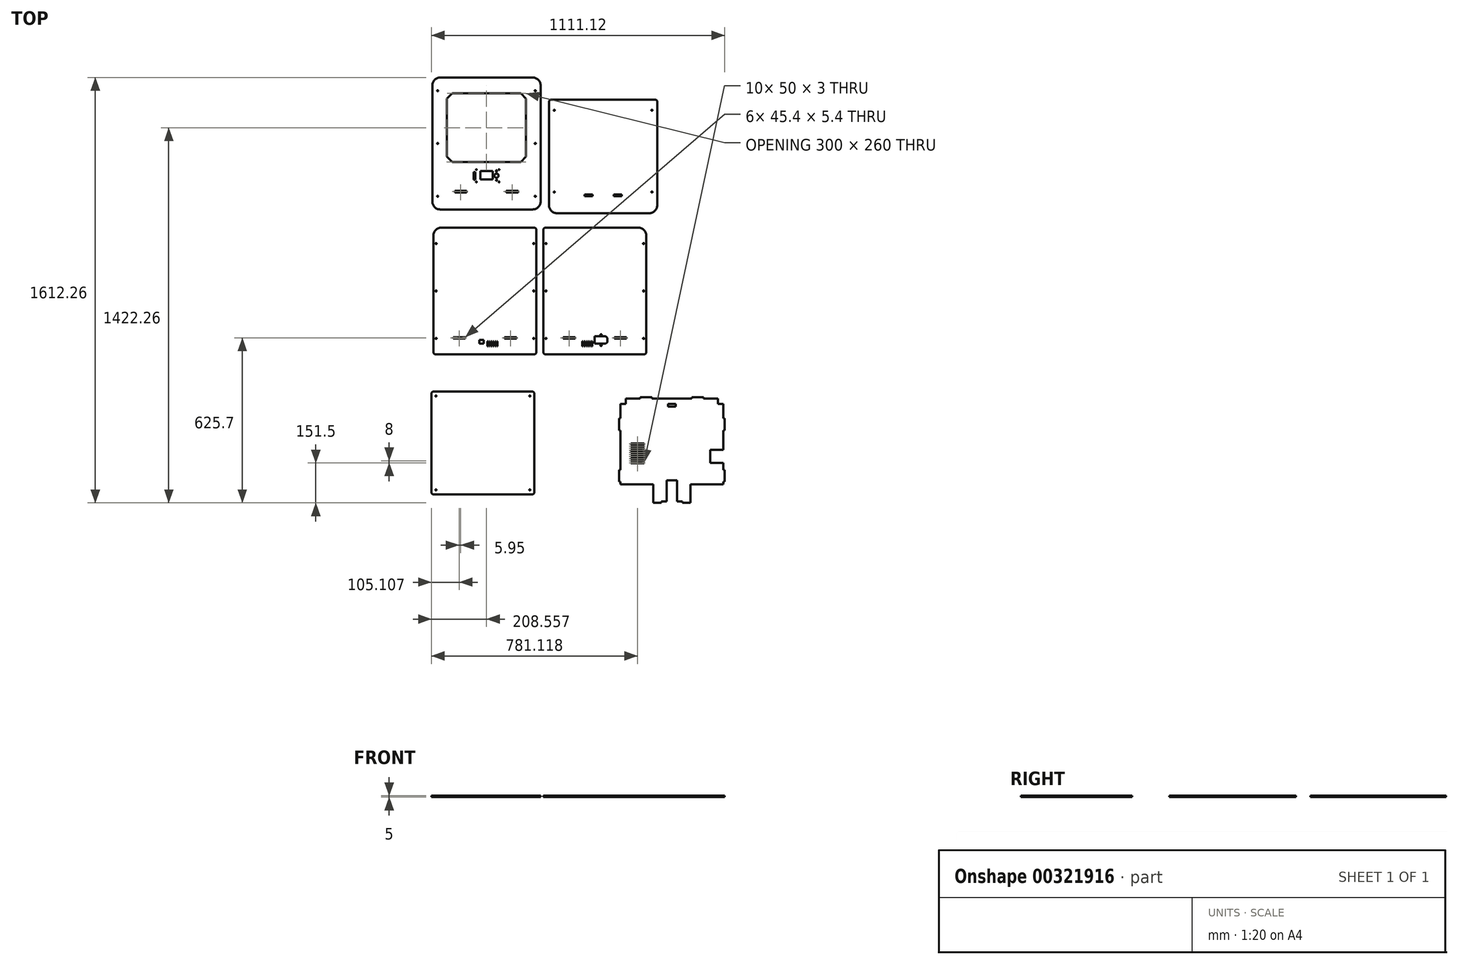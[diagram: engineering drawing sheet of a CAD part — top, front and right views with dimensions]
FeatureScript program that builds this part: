
annotation { "Feature Type Name" : "Feature", "Feature Type Description" : "" }
export const myFeature = defineFeature(function(context is Context, id is Id, definition is map)
    precondition{}
    {
        {
            var Q0;
            Q0=qCreatedBy(makeId("Top.planeOp"),FACE);
            var sketch = newSketch(context, id + "F0", { "sketchPlane" : qUnion([Q0])});
            skLineSegment(sketch, "E0.bottom", {"start": v(-407.26, 527.75) * mm, "end": v(2.74, 527.75) * mm});
            skLineSegment(sketch, "E0.top", {"start": v(-407.26, 27.75) * mm, "end": v(2.74, 27.75) * mm});
            skLineSegment(sketch, "E0.left", {"start": v(-407.26, 527.75) * mm, "end": v(-407.26, 27.75) * mm});
            skLineSegment(sketch, "E0.right", {"start": v(2.74, 527.75) * mm, "end": v(2.74, 27.75) * mm});
            skLineSegment(sketch, "E1.bottom", {"start": v(-352.26, 467.75) * mm, "end": v(-52.26, 467.75) * mm});
            skLineSegment(sketch, "E1.top", {"start": v(-352.26, 207.75) * mm, "end": v(-124.76, 207.75) * mm});
            skLineSegment(sketch, "E1.left", {"start": v(-352.26, 467.75) * mm, "end": v(-352.26, 207.75) * mm});
            skLineSegment(sketch, "E1.right", {"start": v(-52.26, 467.75) * mm, "end": v(-52.26, 207.75) * mm});
            skLineSegment(sketch, "E2", {"start": v(-124.76, 207.75) * mm, "end": v(-52.26, 207.75) * mm});
            skCircle(sketch, "E3", {"center": v(-387.26, 477.75) * mm, "radius": 2.1 * mm});
            skCircle(sketch, "E4", {"center": v(-17.26, 477.75) * mm, "radius": 2.1 * mm});
            skCircle(sketch, "E5", {"center": v(-387.26, 77.75) * mm, "radius": 2.1 * mm});
            skCircle(sketch, "E6", {"center": v(-17.26, 77.75) * mm, "radius": 2.1 * mm});
            skCircle(sketch, "E7", {"center": v(-387.26, 277.75) * mm, "radius": 2.1 * mm});
            skCircle(sketch, "E8", {"center": v(-17.26, 277.75) * mm, "radius": 2.1 * mm});
            skLineSegment(sketch, "E9.bottom", {"start": v(-322.46, 97.95) * mm, "end": v(-277.06, 97.95) * mm});
            skLineSegment(sketch, "E9.top", {"start": v(-322.46, 92.55) * mm, "end": v(-277.06, 92.55) * mm});
            skLineSegment(sketch, "E9.left", {"start": v(-322.46, 97.95) * mm, "end": v(-322.46, 92.55) * mm});
            skLineSegment(sketch, "E9.right", {"start": v(-277.06, 97.95) * mm, "end": v(-277.06, 92.55) * mm});
            skLineSegment(sketch, "E10.bottom", {"start": v(-127.46, 97.95) * mm, "end": v(-82.06, 97.95) * mm});
            skLineSegment(sketch, "E10.top", {"start": v(-127.46, 92.55) * mm, "end": v(-82.06, 92.55) * mm});
            skLineSegment(sketch, "E10.left", {"start": v(-127.46, 97.95) * mm, "end": v(-127.46, 92.55) * mm});
            skLineSegment(sketch, "E10.right", {"start": v(-82.06, 97.95) * mm, "end": v(-82.06, 92.55) * mm});
            skLineSegment(sketch, "E11.bottom", {"start": v(-225.86, 173.25) * mm, "end": v(-178.86, 173.25) * mm});
            skLineSegment(sketch, "E11.top", {"start": v(-225.86, 141.25) * mm, "end": v(-178.86, 141.25) * mm});
            skLineSegment(sketch, "E11.left", {"start": v(-225.86, 173.25) * mm, "end": v(-225.86, 141.25) * mm});
            skLineSegment(sketch, "E11.right", {"start": v(-178.86, 173.25) * mm, "end": v(-178.86, 141.25) * mm});
            skCircle(sketch, "E12", {"center": v(-164.36, 155.75) * mm, "radius": 8 * mm});
            skCircle(sketch, "E13", {"center": v(-164.36, 138.75) * mm, "radius": 2 * mm});
            skLineSegment(sketch, "E14.bottom", {"start": v(-250.86, 169.95) * mm, "end": v(-244.86, 169.95) * mm});
            skLineSegment(sketch, "E14.top", {"start": v(-250.86, 140.75) * mm, "end": v(-244.86, 140.75) * mm});
            skLineSegment(sketch, "E14.left", {"start": v(-250.86, 169.95) * mm, "end": v(-250.86, 140.75) * mm});
            skLineSegment(sketch, "E14.right", {"start": v(-244.86, 169.95) * mm, "end": v(-244.86, 140.75) * mm});
            skCircle(sketch, "E15", {"center": v(-164.36, 173.3) * mm, "radius": 0.6 * mm});
            skCircle(sketch, "E16", {"center": v(-167.36, 173.3) * mm, "radius": 0.6 * mm});
            skCircle(sketch, "E17", {"center": v(-164.36, 170.3) * mm, "radius": 0.6 * mm});
            skCircle(sketch, "E18", {"center": v(-161.36, 173.3) * mm, "radius": 0.6 * mm});
            skCircle(sketch, "E19", {"center": v(-164.36, 176.3) * mm, "radius": 0.6 * mm});
            skCircle(sketch, "E20", {"center": v(-154.56, 178.75) * mm, "radius": 1.6 * mm});
            skCircle(sketch, "E21", {"center": v(-154.56, 131.95) * mm, "radius": 1.6 * mm});
            skCircle(sketch, "E22", {"center": v(-240.56, 131.95) * mm, "radius": 1.6 * mm});
            skCircle(sketch, "E23", {"center": v(-240.56, 178.75) * mm, "radius": 1.6 * mm});
            skSolve(sketch);
        }
        {
            var Q0;
            Q0 = qSketchRegion(id + "F0", true);
            extrude(context, id + "F1", {"entities" : qUnion([Q0]), "offsetDistance" : 25 * mm, "depth" : 5 * mm});
        }
        {
            var Q0;
            Q0=makeQuery(id+"F1.opExtrude","SWEPT_EDGE",EDGE,{"disambiguationData":[OSD([sQuery(id+"F0.wireOp",EDGE,"E0.top"),sQuery(id+"F0.wireOp",EDGE,"E0.left")])]});
            var Q1;
            Q1=makeQuery(id+"F1.opExtrude","SWEPT_EDGE",EDGE,{"disambiguationData":[OSD([sQuery(id+"F0.wireOp",EDGE,"E0.top"),sQuery(id+"F0.wireOp",EDGE,"E0.right")])]});
            var Q2;
            Q2=makeQuery(id+"F1.opExtrude","SWEPT_EDGE",EDGE,{"disambiguationData":[OSD([sQuery(id+"F0.wireOp",EDGE,"E0.bottom"),sQuery(id+"F0.wireOp",EDGE,"E0.left")])]});
            var Q3;
            Q3=makeQuery(id+"F1.opExtrude","SWEPT_EDGE",EDGE,{"disambiguationData":[OSD([sQuery(id+"F0.wireOp",EDGE,"E0.bottom"),sQuery(id+"F0.wireOp",EDGE,"E0.right")])]});
            fillet(context, id + "F2", {"entities" : qUnion([Q0, Q1, Q2, Q3]), "radius" : 30 * mm, "tangentPropagation" : true, "allowEdgeOverflow" : false});
        }
        {
            var Q0;
            Q0=qCreatedBy(makeId("Top.planeOp"),FACE);
            var sketch = newSketch(context, id + "F3", { "sketchPlane" : qUnion([Q0])});
            skLineSegment(sketch, "E24.bottom", {"start": v(34.9, 443.68) * mm, "end": v(444.9, 443.68) * mm});
            skLineSegment(sketch, "E24.top", {"start": v(34.9, 13.68) * mm, "end": v(444.9, 13.68) * mm});
            skLineSegment(sketch, "E24.left", {"start": v(34.9, 443.68) * mm, "end": v(34.9, 13.68) * mm});
            skLineSegment(sketch, "E24.right", {"start": v(444.9, 443.68) * mm, "end": v(444.9, 13.68) * mm});
            skCircle(sketch, "E25", {"center": v(54.9, 403.68) * mm, "radius": 2.1 * mm});
            skCircle(sketch, "E26", {"center": v(424.9, 403.68) * mm, "radius": 2.1 * mm});
            skCircle(sketch, "E27", {"center": v(54.9, 93.68) * mm, "radius": 2.1 * mm});
            skCircle(sketch, "E28", {"center": v(424.9, 93.68) * mm, "radius": 2.1 * mm});
            skLineSegment(sketch, "E29.bottom", {"start": v(169.7, 83.88) * mm, "end": v(200.1, 83.88) * mm});
            skLineSegment(sketch, "E29.top", {"start": v(169.7, 78.48) * mm, "end": v(200.1, 78.48) * mm});
            skLineSegment(sketch, "E29.left", {"start": v(169.7, 83.88) * mm, "end": v(169.7, 78.48) * mm});
            skLineSegment(sketch, "E29.right", {"start": v(200.1, 83.88) * mm, "end": v(200.1, 78.48) * mm});
            skLineSegment(sketch, "E30.bottom", {"start": v(279.7, 83.88) * mm, "end": v(310.1, 83.88) * mm});
            skLineSegment(sketch, "E30.top", {"start": v(279.7, 78.48) * mm, "end": v(310.1, 78.48) * mm});
            skLineSegment(sketch, "E30.left", {"start": v(279.7, 83.88) * mm, "end": v(279.7, 78.48) * mm});
            skLineSegment(sketch, "E30.right", {"start": v(310.1, 83.88) * mm, "end": v(310.1, 78.48) * mm});
            skSolve(sketch);
        }
        {
            var Q0;
            Q0=makeQuery(id+"F1.opExtrude","SWEPT_EDGE",EDGE,{"disambiguationData":[OSD([sQuery(id+"F0.wireOp",EDGE,"E1.bottom"),sQuery(id+"F0.wireOp",EDGE,"E1.left")])]});
            var Q1;
            Q1=makeQuery(id+"F1.opExtrude","SWEPT_EDGE",EDGE,{"disambiguationData":[OSD([sQuery(id+"F0.wireOp",EDGE,"E1.bottom"),sQuery(id+"F0.wireOp",EDGE,"E1.right")])]});
            var Q2;
            Q2=makeQuery(id+"F1.opExtrude","SWEPT_EDGE",EDGE,{"disambiguationData":[OSD([sQuery(id+"F0.wireOp",EDGE,"E1.top"),sQuery(id+"F0.wireOp",EDGE,"E1.left")])]});
            var Q3;
            Q3=makeQuery(id+"F1.opExtrude","SWEPT_EDGE",EDGE,{"disambiguationData":[OSD([sQuery(id+"F0.wireOp",EDGE,"E2"),sQuery(id+"F0.wireOp",EDGE,"4f9qIKP3-aY01-1VRl-neuN-nygdDIXG8IeO")])]});
            chamfer(context, id + "F4", {"entities" : qUnion([Q0, Q1, Q2, Q3]), "width" : 20 * mm, "tangentPropagation" : true});
        }
        {
            var Q0;
            Q0 = qSketchRegion(id + "F3", true);
            extrude(context, id + "F5", {"entities" : qUnion([Q0]), "offsetDistance" : 25 * mm, "depth" : 5 * mm});
        }
        {
            var Q0;
            Q0=makeQuery(id+"F5.opExtrude","SWEPT_EDGE",EDGE,{"disambiguationData":[OSD([sQuery(id+"F3.wireOp",EDGE,"E24.top"),sQuery(id+"F3.wireOp",EDGE,"E24.left")])]});
            var Q1;
            Q1=makeQuery(id+"F5.opExtrude","SWEPT_EDGE",EDGE,{"disambiguationData":[OSD([sQuery(id+"F3.wireOp",EDGE,"E24.top"),sQuery(id+"F3.wireOp",EDGE,"E24.right")])]});
            fillet(context, id + "F6", {"entities" : qUnion([Q0, Q1]), "radius" : 30 * mm, "tangentPropagation" : true, "allowEdgeOverflow" : false});
        }
        {
            var Q0;
            Q0=qCreatedBy(makeId("Top.planeOp"),FACE);
            var sketch = newSketch(context, id + "F7", { "sketchPlane" : qUnion([Q0])});
            skLineSegment(sketch, "E31.bottom", {"start": v(-13.21, -41.3) * mm, "end": v(-403.21, -41.3) * mm});
            skLineSegment(sketch, "E31.top", {"start": v(-13.21, -521.3) * mm, "end": v(-403.21, -521.3) * mm});
            skLineSegment(sketch, "E31.left", {"start": v(-13.21, -41.3) * mm, "end": v(-13.21, -136.3) * mm});
            skLineSegment(sketch, "E31.right", {"start": v(-403.21, -41.3) * mm, "end": v(-403.21, -136.3) * mm});
            skLineSegment(sketch, "E32.trimOffspring", {"start": v(-13.21, -158.3) * mm, "end": v(-13.21, -521.3) * mm});
            skLineSegment(sketch, "E33.trimOffspring", {"start": v(-403.21, -158.3) * mm, "end": v(-403.21, -521.3) * mm});
            skCircle(sketch, "E34", {"center": v(-393.21, -101.3) * mm, "radius": 2.1 * mm});
            skCircle(sketch, "E35", {"center": v(-23.21, -101.3) * mm, "radius": 2.1 * mm});
            skCircle(sketch, "E36", {"center": v(-393.21, -461.3) * mm, "radius": 2.1 * mm});
            skCircle(sketch, "E37", {"center": v(-23.21, -461.3) * mm, "radius": 2.1 * mm});
            skCircle(sketch, "E38", {"center": v(-393.21, -281.3) * mm, "radius": 2.1 * mm});
            skCircle(sketch, "E39", {"center": v(-23.21, -281.3) * mm, "radius": 2.1 * mm});
            skLineSegment(sketch, "E40", {"start": v(-13.21, -158.3) * mm, "end": v(-13.21, -136.3) * mm});
            skLineSegment(sketch, "E41", {"start": v(-403.21, -158.3) * mm, "end": v(-403.21, -136.3) * mm});
            skLineSegment(sketch, "E42.bottom", {"start": v(-229.21, -467.3) * mm, "end": v(-213.21, -467.3) * mm});
            skLineSegment(sketch, "E42.top", {"start": v(-229.21, -481.3) * mm, "end": v(-213.21, -481.3) * mm});
            skLineSegment(sketch, "E42.left", {"start": v(-229.21, -467.3) * mm, "end": v(-229.21, -481.3) * mm});
            skLineSegment(sketch, "E42.right", {"start": v(-213.21, -467.3) * mm, "end": v(-213.21, -481.3) * mm});
            skLineSegment(sketch, "E43.bottom", {"start": v(-328.41, -456.1) * mm, "end": v(-283.01, -456.1) * mm});
            skLineSegment(sketch, "E43.top", {"start": v(-328.41, -461.5) * mm, "end": v(-283.01, -461.5) * mm});
            skLineSegment(sketch, "E43.left", {"start": v(-328.41, -456.1) * mm, "end": v(-328.41, -461.5) * mm});
            skLineSegment(sketch, "E43.right", {"start": v(-283.01, -456.1) * mm, "end": v(-283.01, -461.5) * mm});
            skLineSegment(sketch, "E44.bottom", {"start": v(-133.41, -456.1) * mm, "end": v(-88.01, -456.1) * mm});
            skLineSegment(sketch, "E44.top", {"start": v(-133.41, -461.5) * mm, "end": v(-88.01, -461.5) * mm});
            skLineSegment(sketch, "E44.left", {"start": v(-133.41, -456.1) * mm, "end": v(-133.41, -461.5) * mm});
            skLineSegment(sketch, "E44.right", {"start": v(-88.01, -456.1) * mm, "end": v(-88.01, -461.5) * mm});
            skLineSegment(sketch, "E45.bottom", {"start": v(-198.21, -471.3) * mm, "end": v(-195.21, -471.3) * mm});
            skLineSegment(sketch, "E45.top", {"start": v(-198.21, -491.3) * mm, "end": v(-195.21, -491.3) * mm});
            skLineSegment(sketch, "E45.left", {"start": v(-198.21, -471.3) * mm, "end": v(-198.21, -491.3) * mm});
            skLineSegment(sketch, "E45.right", {"start": v(-195.21, -471.3) * mm, "end": v(-195.21, -491.3) * mm});
            skLineSegment(sketch, "E46.bottom", {"start": v(-191.21, -471.3) * mm, "end": v(-188.21, -471.3) * mm});
            skLineSegment(sketch, "E46.top", {"start": v(-191.21, -491.3) * mm, "end": v(-188.21, -491.3) * mm});
            skLineSegment(sketch, "E46.left", {"start": v(-191.21, -471.3) * mm, "end": v(-191.21, -491.3) * mm});
            skLineSegment(sketch, "E46.right", {"start": v(-188.21, -471.3) * mm, "end": v(-188.21, -491.3) * mm});
            skLineSegment(sketch, "E47.bottom", {"start": v(-184.21, -471.3) * mm, "end": v(-181.21, -471.3) * mm});
            skLineSegment(sketch, "E47.top", {"start": v(-184.21, -491.3) * mm, "end": v(-181.21, -491.3) * mm});
            skLineSegment(sketch, "E47.left", {"start": v(-184.21, -471.3) * mm, "end": v(-184.21, -491.3) * mm});
            skLineSegment(sketch, "E47.right", {"start": v(-181.21, -471.3) * mm, "end": v(-181.21, -491.3) * mm});
            skLineSegment(sketch, "E48.bottom", {"start": v(-177.21, -471.3) * mm, "end": v(-174.21, -471.3) * mm});
            skLineSegment(sketch, "E48.top", {"start": v(-177.21, -491.3) * mm, "end": v(-174.21, -491.3) * mm});
            skLineSegment(sketch, "E48.left", {"start": v(-177.21, -471.3) * mm, "end": v(-177.21, -491.3) * mm});
            skLineSegment(sketch, "E48.right", {"start": v(-174.21, -471.3) * mm, "end": v(-174.21, -491.3) * mm});
            skLineSegment(sketch, "E49.bottom", {"start": v(-170.21, -471.3) * mm, "end": v(-167.21, -471.3) * mm});
            skLineSegment(sketch, "E49.top", {"start": v(-170.21, -491.3) * mm, "end": v(-167.21, -491.3) * mm});
            skLineSegment(sketch, "E49.left", {"start": v(-170.21, -471.3) * mm, "end": v(-170.21, -491.3) * mm});
            skLineSegment(sketch, "E49.right", {"start": v(-167.21, -471.3) * mm, "end": v(-167.21, -491.3) * mm});
            skLineSegment(sketch, "E50.bottom", {"start": v(-163.21, -471.3) * mm, "end": v(-160.21, -471.3) * mm});
            skLineSegment(sketch, "E50.top", {"start": v(-163.21, -491.3) * mm, "end": v(-160.21, -491.3) * mm});
            skLineSegment(sketch, "E50.left", {"start": v(-163.21, -471.3) * mm, "end": v(-163.21, -491.3) * mm});
            skLineSegment(sketch, "E50.right", {"start": v(-160.21, -471.3) * mm, "end": v(-160.21, -491.3) * mm});
            skSolve(sketch);
        }
        {
            var Q0;
            {var subQ5=sQuery(id+"F7.wireOp",EDGE,"E31.bottom");Q0=makeQuery(id+"F7.imprint","IMPRINT",FACE,{"disambiguationData":[TD([[makeQuery(id+"F7.imprint","IMPRINT",EDGE,{"derivedFrom":subQ5}),1.0]])]});}
            extrude(context, id + "F8", {"entities" : qUnion([Q0]), "offsetDistance" : 25 * mm, "depth" : 5 * mm});
        }
        {
            var Q0;
            Q0=makeQuery(id+"F8.opExtrude","SWEPT_EDGE",EDGE,{"disambiguationData":[OSD([sQuery(id+"F7.wireOp",EDGE,"E31.bottom"),sQuery(id+"F7.wireOp",EDGE,"E31.right")])]});
            fillet(context, id + "F9", {"entities" : qUnion([Q0]), "radius" : 30 * mm, "tangentPropagation" : true, "allowEdgeOverflow" : false});
        }
        {
            var Q0;
            Q0=makeQuery(id+"F8.opExtrude","SWEPT_BODY",BODY,{"disambiguationData":[OSD([sQuery(id+"F7.wireOp",EDGE,"E31.bottom"),sQuery(id+"F7.wireOp",EDGE,"E31.top"),sQuery(id+"F7.wireOp",EDGE,"E31.left"),sQuery(id+"F7.wireOp",EDGE,"E31.right"),sQuery(id+"F7.wireOp",EDGE,"LNA97dMV-EioV-m8da-z8l0-Q8Sx3lvQ8D6H.bottom"),sQuery(id+"F7.wireOp",EDGE,"LNA97dMV-EioV-m8da-z8l0-Q8Sx3lvQ8D6H.top"),sQuery(id+"F7.wireOp",EDGE,"LNA97dMV-EioV-m8da-z8l0-Q8Sx3lvQ8D6H.left"),sQuery(id+"F7.wireOp",EDGE,"LNA97dMV-EioV-m8da-z8l0-Q8Sx3lvQ8D6H.right"),sQuery(id+"F7.wireOp",EDGE,"giE2yFys-hD4j-tFcK-ibZG-6tEsuw6JLsj2.bottom"),sQuery(id+"F7.wireOp",EDGE,"giE2yFys-hD4j-tFcK-ibZG-6tEsuw6JLsj2.top"),sQuery(id+"F7.wireOp",EDGE,"giE2yFys-hD4j-tFcK-ibZG-6tEsuw6JLsj2.right")])]});
            var Q1;
            Q1=qCreatedBy(makeId("Right.planeOp"),FACE);
            mirror(context, id + "F10", {"entities" : qUnion([Q0]), "mirrorPlane" : qUnion([Q1])});
        }
        {
            var Q0;
            Q0=makeQuery(id+"F10.opPattern","COPY",FACE,{"derivedFrom":makeQuery(id+"F8.opExtrude","CAP_FACE",FACE,{"disambiguationData":[OSD([sQuery(id+"F7.wireOp",EDGE,"E31.bottom"),sQuery(id+"F7.wireOp",EDGE,"E31.top"),sQuery(id+"F7.wireOp",EDGE,"E31.left"),sQuery(id+"F7.wireOp",EDGE,"E31.right"),sQuery(id+"F7.wireOp",EDGE,"LNA97dMV-EioV-m8da-z8l0-Q8Sx3lvQ8D6H.bottom"),sQuery(id+"F7.wireOp",EDGE,"LNA97dMV-EioV-m8da-z8l0-Q8Sx3lvQ8D6H.top"),sQuery(id+"F7.wireOp",EDGE,"LNA97dMV-EioV-m8da-z8l0-Q8Sx3lvQ8D6H.left"),sQuery(id+"F7.wireOp",EDGE,"LNA97dMV-EioV-m8da-z8l0-Q8Sx3lvQ8D6H.right"),sQuery(id+"F7.wireOp",EDGE,"giE2yFys-hD4j-tFcK-ibZG-6tEsuw6JLsj2.bottom"),sQuery(id+"F7.wireOp",EDGE,"giE2yFys-hD4j-tFcK-ibZG-6tEsuw6JLsj2.top"),sQuery(id+"F7.wireOp",EDGE,"giE2yFys-hD4j-tFcK-ibZG-6tEsuw6JLsj2.right")])],"isStart":true}),"instanceName":"1"});
            var sketch = newSketch(context, id + "F11", { "sketchPlane" : qUnion([Q0])});
            skLineSegment(sketch, "E51.bottom", {"start": v(256.21, 453.3) * mm, "end": v(208.21, 453.3) * mm});
            skLineSegment(sketch, "E51.top", {"start": v(256.21, 481.3) * mm, "end": v(208.21, 481.3) * mm});
            skLineSegment(sketch, "E51.left", {"start": v(256.21, 453.3) * mm, "end": v(256.21, 481.3) * mm});
            skLineSegment(sketch, "E51.right", {"start": v(208.21, 453.3) * mm, "end": v(208.21, 481.3) * mm});
            skCircle(sketch, "E52", {"center": v(232.21, 447.3) * mm, "radius": 2.4 * mm});
            skPoint(sketch, "E52.centerSnap0", {"position": v(232.21, 453.3) * mm});
            skCircle(sketch, "E53", {"center": v(232.21, 487.3) * mm, "radius": 2.4 * mm});
            skSolve(sketch);
        }
        {
            var Q0;
            Q0=makeQuery(id+"F11.imprint","IMPRINT",FACE,{"disambiguationData":[TD([[makeQuery(id+"F11.imprint","IMPRINT",EDGE,{"derivedFrom":sQuery(id+"F11.wireOp",EDGE,"E51.bottom")}),-1.0]])]});
            var Q1;
            Q1=makeQuery(id+"F11.imprint","IMPRINT",FACE,{"disambiguationData":[TD([[makeQuery(id+"F11.imprint","IMPRINT",EDGE,{"derivedFrom":sQuery(id+"F11.wireOp",EDGE,"E52")}),1.0]])]});
            var Q2;
            Q2=makeQuery(id+"F11.imprint","IMPRINT",FACE,{"disambiguationData":[TD([[makeQuery(id+"F11.imprint","IMPRINT",EDGE,{"derivedFrom":sQuery(id+"F11.wireOp",EDGE,"E53")}),1.0]])]});
            var Q3;
            {var subQ0=sQuery(id+"F11.wireOp",EDGE,"pQkS5TOP-vqAZ-noVF-weTm-LPDR1NZVyJVr.top");Q3=makeQuery(id+"F11.imprint","IMPRINT",FACE,{"disambiguationData":[TD([[makeQuery(id+"F11.imprint","IMPRINT",EDGE,{"derivedFrom":subQ0}),-1.0]])]});}
            extrude(context, id + "F12", {"entities" : qUnion([Q0, Q1, Q2, Q3]), "operationType" : NewBodyOperationType.REMOVE, "endBound" : BoundingType.THROUGH_ALL, "oppositeDirection" : true, "depth" : 25 * mm, "offsetDistance" : 25 * mm});
        }
        {
            var Q0;
            Q0=makeQuery(id+"F12.boolean.opBoolean","COPY",EDGE,{"derivedFrom":makeQuery(id+"F12.opExtrude","SWEPT_EDGE",EDGE,{"disambiguationData":[OSD([sQuery(id+"F11.wireOp",EDGE,"E51.bottom"),sQuery(id+"F11.wireOp",EDGE,"E51.left")])]})});
            var Q1;
            Q1=makeQuery(id+"F12.boolean.opBoolean","COPY",EDGE,{"derivedFrom":makeQuery(id+"F12.opExtrude","SWEPT_EDGE",EDGE,{"disambiguationData":[OSD([sQuery(id+"F11.wireOp",EDGE,"E51.top"),sQuery(id+"F11.wireOp",EDGE,"E51.left")])]})});
            chamfer(context, id + "F13", {"entities" : qUnion([Q0, Q1]), "width" : 6 * mm, "tangentPropagation" : true});
        }
        {
            var Q0;
            Q0=qCreatedBy(makeId("Top.planeOp"),FACE);
            var sketch = newSketch(context, id + "F14", { "sketchPlane" : qUnion([Q0])});
            skLineSegment(sketch, "E54.bottom", {"start": v(-410.82, -662.11) * mm, "end": v(-20.82, -662.11) * mm});
            skLineSegment(sketch, "E54.top", {"start": v(-410.82, -1052.11) * mm, "end": v(-20.82, -1052.11) * mm});
            skLineSegment(sketch, "E54.left", {"start": v(-410.82, -662.11) * mm, "end": v(-410.82, -1052.11) * mm});
            skLineSegment(sketch, "E54.right", {"start": v(-20.82, -662.11) * mm, "end": v(-20.82, -1052.11) * mm});
            skCircle(sketch, "E55", {"center": v(-393.82, -679.11) * mm, "radius": 2.1 * mm});
            skCircle(sketch, "E56", {"center": v(-37.82, -679.11) * mm, "radius": 2.1 * mm});
            skCircle(sketch, "E57", {"center": v(-393.82, -1035.11) * mm, "radius": 2.1 * mm});
            skCircle(sketch, "E58", {"center": v(-37.82, -1035.11) * mm, "radius": 2.1 * mm});
            skSolve(sketch);
        }
        {
            var Q0;
            Q0 = qSketchRegion(id + "F14", true);
            extrude(context, id + "F15", {"entities" : qUnion([Q0]), "offsetDistance" : 25 * mm, "depth" : 5 * mm});
        }
        {
            var Q0;
            Q0=qCreatedBy(makeId("Top.planeOp"),FACE);
            var sketch = newSketch(context, id + "F16", { "sketchPlane" : qUnion([Q0])});
            skLineSegment(sketch, "E59.bottom", {"start": v(325.3, -689.51) * mm, "end": v(675.3, -689.51) * mm});
            skLineSegment(sketch, "E59.top", {"start": v(430.3, -1079.51) * mm, "end": v(480.3, -1079.51) * mm});
            skLineSegment(sketch, "E59.left", {"start": v(305.3, -709.51) * mm, "end": v(305.3, -1014.51) * mm});
            skLineSegment(sketch, "E59.right", {"start": v(695.3, -709.51) * mm, "end": v(695.3, -883.01) * mm});
            skLineSegment(sketch, "E60", {"start": v(305.3, -709.51) * mm, "end": v(325.3, -709.51) * mm});
            skLineSegment(sketch, "E61", {"start": v(325.3, -709.51) * mm, "end": v(325.3, -689.51) * mm});
            skLineSegment(sketch, "E62", {"start": v(305.3, -1014.51) * mm, "end": v(430.3, -1014.51) * mm});
            skLineSegment(sketch, "E63", {"start": v(430.3, -1014.51) * mm, "end": v(430.3, -1079.51) * mm});
            skLineSegment(sketch, "E64", {"start": v(675.3, -689.51) * mm, "end": v(675.3, -709.51) * mm});
            skLineSegment(sketch, "E65", {"start": v(675.3, -709.51) * mm, "end": v(695.3, -709.51) * mm});
            skLineSegment(sketch, "E66", {"start": v(695.3, -1014.51) * mm, "end": v(570.3, -1014.51) * mm});
            skLineSegment(sketch, "E67", {"start": v(570.3, -1014.51) * mm, "end": v(570.3, -1079.51) * mm});
            skPoint(sketch, "E68.orphan", {"position": v(305.3, -1079.51) * mm});
            skLineSegment(sketch, "E69", {"start": v(480.3, -1079.51) * mm, "end": v(480.3, -999.51) * mm});
            skLineSegment(sketch, "E70", {"start": v(480.3, -999.51) * mm, "end": v(520.3, -999.51) * mm});
            skLineSegment(sketch, "E71", {"start": v(520.3, -999.51) * mm, "end": v(520.3, -1079.51) * mm});
            skLineSegment(sketch, "E72.trimOffspring", {"start": v(520.3, -1079.51) * mm, "end": v(570.3, -1079.51) * mm});
            skLineSegment(sketch, "E73", {"start": v(695.3, -933.01) * mm, "end": v(645.3, -933.01) * mm});
            skLineSegment(sketch, "E74", {"start": v(645.3, -933.01) * mm, "end": v(645.3, -883.01) * mm});
            skLineSegment(sketch, "E75", {"start": v(645.3, -883.01) * mm, "end": v(695.3, -883.01) * mm});
            skLineSegment(sketch, "E76.trimOffspring", {"start": v(695.3, -933.01) * mm, "end": v(695.3, -1014.51) * mm});
            skLineSegment(sketch, "E77.bottom", {"start": v(485.3, -709.51) * mm, "end": v(515.3, -709.51) * mm});
            skLineSegment(sketch, "E77.top", {"start": v(485.3, -719.51) * mm, "end": v(515.3, -719.51) * mm});
            skLineSegment(sketch, "E77.left", {"start": v(485.3, -709.51) * mm, "end": v(485.3, -719.51) * mm});
            skLineSegment(sketch, "E77.right", {"start": v(515.3, -709.51) * mm, "end": v(515.3, -719.51) * mm});
            skLineSegment(sketch, "E78", {"start": v(380.3, -689.51) * mm, "end": v(380.3, -684.51) * mm});
            skLineSegment(sketch, "E79", {"start": v(380.3, -684.51) * mm, "end": v(425.3, -684.51) * mm});
            skLineSegment(sketch, "E80", {"start": v(425.3, -684.51) * mm, "end": v(425.3, -689.51) * mm});
            skLineSegment(sketch, "E81", {"start": v(575.3, -689.51) * mm, "end": v(575.3, -684.51) * mm});
            skLineSegment(sketch, "E82", {"start": v(575.3, -684.51) * mm, "end": v(620.3, -684.51) * mm});
            skLineSegment(sketch, "E83", {"start": v(620.3, -684.51) * mm, "end": v(620.3, -689.51) * mm});
            skLineSegment(sketch, "E84", {"start": v(695.3, -764.51) * mm, "end": v(700.3, -764.51) * mm});
            skLineSegment(sketch, "E85", {"start": v(700.3, -764.51) * mm, "end": v(700.3, -809.51) * mm});
            skLineSegment(sketch, "E86", {"start": v(700.3, -809.51) * mm, "end": v(695.3, -809.51) * mm});
            skLineSegment(sketch, "E87", {"start": v(695.3, -959.51) * mm, "end": v(700.3, -959.51) * mm});
            skLineSegment(sketch, "E88", {"start": v(700.3, -959.51) * mm, "end": v(700.3, -1004.51) * mm});
            skLineSegment(sketch, "E89", {"start": v(700.3, -1004.51) * mm, "end": v(695.3, -1004.51) * mm});
            skLineSegment(sketch, "E90", {"start": v(540.3, -1079.51) * mm, "end": v(540.3, -1084.51) * mm});
            skLineSegment(sketch, "E91", {"start": v(540.3, -1084.51) * mm, "end": v(570.3, -1084.51) * mm});
            skLineSegment(sketch, "E92", {"start": v(570.3, -1084.51) * mm, "end": v(570.3, -1079.51) * mm});
            skLineSegment(sketch, "E93", {"start": v(430.3, -1079.51) * mm, "end": v(430.3, -1084.51) * mm});
            skLineSegment(sketch, "E94", {"start": v(430.3, -1084.51) * mm, "end": v(460.3, -1084.51) * mm});
            skLineSegment(sketch, "E95", {"start": v(460.3, -1084.51) * mm, "end": v(460.3, -1079.51) * mm});
            skLineSegment(sketch, "E96", {"start": v(305.3, -764.51) * mm, "end": v(300.3, -764.51) * mm});
            skLineSegment(sketch, "E97", {"start": v(300.3, -764.51) * mm, "end": v(300.3, -809.51) * mm});
            skLineSegment(sketch, "E98", {"start": v(300.3, -809.51) * mm, "end": v(305.3, -809.51) * mm});
            skLineSegment(sketch, "E99", {"start": v(305.3, -959.51) * mm, "end": v(300.3, -959.51) * mm});
            skLineSegment(sketch, "E100", {"start": v(300.3, -959.51) * mm, "end": v(300.3, -1004.51) * mm});
            skLineSegment(sketch, "E101", {"start": v(300.3, -1004.51) * mm, "end": v(305.3, -1004.51) * mm});
            skLineSegment(sketch, "E102.bottom", {"start": v(345.3, -859.51) * mm, "end": v(395.3, -859.51) * mm});
            skLineSegment(sketch, "E102.top", {"start": v(345.3, -862.51) * mm, "end": v(395.3, -862.51) * mm});
            skLineSegment(sketch, "E102.left", {"start": v(345.3, -859.51) * mm, "end": v(345.3, -862.51) * mm});
            skLineSegment(sketch, "E102.right", {"start": v(395.3, -859.51) * mm, "end": v(395.3, -862.51) * mm});
            skLineSegment(sketch, "E103.0.1.0", {"start": v(345.3, -870.51) * mm, "end": v(395.3, -870.51) * mm});
            skLineSegment(sketch, "E103.0.1.1", {"start": v(345.3, -867.51) * mm, "end": v(395.3, -867.51) * mm});
            skLineSegment(sketch, "E103.0.1.2", {"start": v(395.3, -867.51) * mm, "end": v(395.3, -870.51) * mm});
            skLineSegment(sketch, "E103.0.1.3", {"start": v(345.3, -867.51) * mm, "end": v(345.3, -870.51) * mm});
            skLineSegment(sketch, "E103.0.2.0", {"start": v(345.3, -878.51) * mm, "end": v(395.3, -878.51) * mm});
            skLineSegment(sketch, "E103.0.2.1", {"start": v(345.3, -875.51) * mm, "end": v(395.3, -875.51) * mm});
            skLineSegment(sketch, "E103.0.2.2", {"start": v(395.3, -875.51) * mm, "end": v(395.3, -878.51) * mm});
            skLineSegment(sketch, "E103.0.2.3", {"start": v(345.3, -875.51) * mm, "end": v(345.3, -878.51) * mm});
            skLineSegment(sketch, "E103.0.3.0", {"start": v(345.3, -886.51) * mm, "end": v(395.3, -886.51) * mm});
            skLineSegment(sketch, "E103.0.3.1", {"start": v(345.3, -883.51) * mm, "end": v(395.3, -883.51) * mm});
            skLineSegment(sketch, "E103.0.3.2", {"start": v(395.3, -883.51) * mm, "end": v(395.3, -886.51) * mm});
            skLineSegment(sketch, "E103.0.3.3", {"start": v(345.3, -883.51) * mm, "end": v(345.3, -886.51) * mm});
            skLineSegment(sketch, "E103.0.4.0", {"start": v(345.3, -894.51) * mm, "end": v(395.3, -894.51) * mm});
            skLineSegment(sketch, "E103.0.4.1", {"start": v(345.3, -891.51) * mm, "end": v(395.3, -891.51) * mm});
            skLineSegment(sketch, "E103.0.4.2", {"start": v(395.3, -891.51) * mm, "end": v(395.3, -894.51) * mm});
            skLineSegment(sketch, "E103.0.4.3", {"start": v(345.3, -891.51) * mm, "end": v(345.3, -894.51) * mm});
            skLineSegment(sketch, "E103.0.5.0", {"start": v(345.3, -902.51) * mm, "end": v(395.3, -902.51) * mm});
            skLineSegment(sketch, "E103.0.5.1", {"start": v(345.3, -899.51) * mm, "end": v(395.3, -899.51) * mm});
            skLineSegment(sketch, "E103.0.5.2", {"start": v(395.3, -899.51) * mm, "end": v(395.3, -902.51) * mm});
            skLineSegment(sketch, "E103.0.5.3", {"start": v(345.3, -899.51) * mm, "end": v(345.3, -902.51) * mm});
            skLineSegment(sketch, "E103.0.6.0", {"start": v(345.3, -910.51) * mm, "end": v(395.3, -910.51) * mm});
            skLineSegment(sketch, "E103.0.6.1", {"start": v(345.3, -907.51) * mm, "end": v(395.3, -907.51) * mm});
            skLineSegment(sketch, "E103.0.6.2", {"start": v(395.3, -907.51) * mm, "end": v(395.3, -910.51) * mm});
            skLineSegment(sketch, "E103.0.6.3", {"start": v(345.3, -907.51) * mm, "end": v(345.3, -910.51) * mm});
            skLineSegment(sketch, "E103.0.7.0", {"start": v(345.3, -918.51) * mm, "end": v(395.3, -918.51) * mm});
            skLineSegment(sketch, "E103.0.7.1", {"start": v(345.3, -915.51) * mm, "end": v(395.3, -915.51) * mm});
            skLineSegment(sketch, "E103.0.7.2", {"start": v(395.3, -915.51) * mm, "end": v(395.3, -918.51) * mm});
            skLineSegment(sketch, "E103.0.7.3", {"start": v(345.3, -915.51) * mm, "end": v(345.3, -918.51) * mm});
            skLineSegment(sketch, "E103.0.8.0", {"start": v(345.3, -926.51) * mm, "end": v(395.3, -926.51) * mm});
            skLineSegment(sketch, "E103.0.8.1", {"start": v(345.3, -923.51) * mm, "end": v(395.3, -923.51) * mm});
            skLineSegment(sketch, "E103.0.8.2", {"start": v(395.3, -923.51) * mm, "end": v(395.3, -926.51) * mm});
            skLineSegment(sketch, "E103.0.8.3", {"start": v(345.3, -923.51) * mm, "end": v(345.3, -926.51) * mm});
            skLineSegment(sketch, "E103.0.9.0", {"start": v(345.3, -934.51) * mm, "end": v(395.3, -934.51) * mm});
            skLineSegment(sketch, "E103.0.9.1", {"start": v(345.3, -931.51) * mm, "end": v(395.3, -931.51) * mm});
            skLineSegment(sketch, "E103.0.9.2", {"start": v(395.3, -931.51) * mm, "end": v(395.3, -934.51) * mm});
            skLineSegment(sketch, "E103.0.9.3", {"start": v(345.3, -931.51) * mm, "end": v(345.3, -934.51) * mm});
            skLineSegment(sketch, "E103.direction1", {"start": v(345.3, -862.51) * mm, "end": v(370.3, -862.51) * mm, "construction": true});
            skLineSegment(sketch, "E103.direction2", {"start": v(345.3, -862.51) * mm, "end": v(345.3, -870.51) * mm, "construction": true});
            skSolve(sketch);
        }
        {
            var Q0;
            Q0=makeQuery(id+"F16.imprint","IMPRINT",FACE,{"disambiguationData":[TD([[makeQuery(id+"F16.imprint","IMPRINT",EDGE,{"derivedFrom":sQuery(id+"F16.wireOp",EDGE,"E59.bottom")}),-1.0]])]});
            var Q1;
            {var subQ0=sQuery(id+"F16.wireOp",EDGE,"E78");Q1=makeQuery(id+"F16.imprint","IMPRINT",FACE,{"disambiguationData":[TD([[makeQuery(id+"F16.imprint","IMPRINT",EDGE,{"derivedFrom":subQ0}),-1.0]])]});}
            var Q2;
            {var subQ0=sQuery(id+"F16.wireOp",EDGE,"E96");Q2=makeQuery(id+"F16.imprint","IMPRINT",FACE,{"disambiguationData":[TD([[makeQuery(id+"F16.imprint","IMPRINT",EDGE,{"derivedFrom":subQ0}),1.0]])]});}
            var Q3;
            {var subQ0=sQuery(id+"F16.wireOp",EDGE,"E81");Q3=makeQuery(id+"F16.imprint","IMPRINT",FACE,{"disambiguationData":[TD([[makeQuery(id+"F16.imprint","IMPRINT",EDGE,{"derivedFrom":subQ0}),-1.0]])]});}
            var Q4;
            {var subQ0=sQuery(id+"F16.wireOp",EDGE,"E84");Q4=makeQuery(id+"F16.imprint","IMPRINT",FACE,{"disambiguationData":[TD([[makeQuery(id+"F16.imprint","IMPRINT",EDGE,{"derivedFrom":subQ0}),-1.0]])]});}
            var Q5;
            {var subQ0=sQuery(id+"F16.wireOp",EDGE,"E87");Q5=makeQuery(id+"F16.imprint","IMPRINT",FACE,{"disambiguationData":[TD([[makeQuery(id+"F16.imprint","IMPRINT",EDGE,{"derivedFrom":subQ0}),-1.0]])]});}
            var Q6;
            {var subQ0=sQuery(id+"F16.wireOp",EDGE,"E90");Q6=makeQuery(id+"F16.imprint","IMPRINT",FACE,{"disambiguationData":[TD([[makeQuery(id+"F16.imprint","IMPRINT",EDGE,{"derivedFrom":subQ0}),1.0]])]});}
            var Q7;
            {var subQ0=sQuery(id+"F16.wireOp",EDGE,"E93");Q7=makeQuery(id+"F16.imprint","IMPRINT",FACE,{"disambiguationData":[TD([[makeQuery(id+"F16.imprint","IMPRINT",EDGE,{"derivedFrom":subQ0}),1.0]])]});}
            var Q8;
            {var subQ0=sQuery(id+"F16.wireOp",EDGE,"E99");Q8=makeQuery(id+"F16.imprint","IMPRINT",FACE,{"disambiguationData":[TD([[makeQuery(id+"F16.imprint","IMPRINT",EDGE,{"derivedFrom":subQ0}),1.0]])]});}
            extrude(context, id + "F17", {"entities" : qUnion([Q0, Q1, Q2, Q3, Q4, Q5, Q6, Q7, Q8]), "depth" : 5 * mm, "offsetDistance" : 25 * mm});
        }
        {
            var Q0;
            Q0=makeQuery(id+"F5.opExtrude","SWEPT_EDGE",EDGE,{"disambiguationData":[OSD([sQuery(id+"F3.wireOp",EDGE,"E24.bottom"),sQuery(id+"F3.wireOp",EDGE,"E24.right")])]});
            var Q1;
            Q1=makeQuery(id+"F5.opExtrude","SWEPT_EDGE",EDGE,{"disambiguationData":[OSD([sQuery(id+"F3.wireOp",EDGE,"E24.bottom"),sQuery(id+"F3.wireOp",EDGE,"E24.left")])]});
            var Q2;
            Q2=makeQuery(id+"F8.opExtrude","SWEPT_EDGE",EDGE,{"disambiguationData":[OSD([sQuery(id+"F7.wireOp",EDGE,"E31.bottom"),sQuery(id+"F7.wireOp",EDGE,"E31.left")])]});
            var Q3;
            Q3=makeQuery(id+"F10.opPattern","COPY",EDGE,{"derivedFrom":makeQuery(id+"F8.opExtrude","SWEPT_EDGE",EDGE,{"disambiguationData":[OSD([sQuery(id+"F7.wireOp",EDGE,"E31.bottom"),sQuery(id+"F7.wireOp",EDGE,"E31.left")])]}),"instanceName":"1"});
            var Q4;
            Q4=makeQuery(id+"F10.opPattern","COPY",EDGE,{"derivedFrom":makeQuery(id+"F8.opExtrude","SWEPT_EDGE",EDGE,{"disambiguationData":[OSD([sQuery(id+"F7.wireOp",EDGE,"E31.top"),sQuery(id+"F7.wireOp",EDGE,"E33.trimOffspring")])]}),"instanceName":"1"});
            var Q5;
            Q5=makeQuery(id+"F10.opPattern","COPY",EDGE,{"derivedFrom":makeQuery(id+"F8.opExtrude","SWEPT_EDGE",EDGE,{"disambiguationData":[OSD([sQuery(id+"F7.wireOp",EDGE,"E31.top"),sQuery(id+"F7.wireOp",EDGE,"E32.trimOffspring")])]}),"instanceName":"1"});
            var Q6;
            Q6=makeQuery(id+"F8.opExtrude","SWEPT_EDGE",EDGE,{"disambiguationData":[OSD([sQuery(id+"F7.wireOp",EDGE,"E31.top"),sQuery(id+"F7.wireOp",EDGE,"E32.trimOffspring")])]});
            var Q7;
            Q7=makeQuery(id+"F8.opExtrude","SWEPT_EDGE",EDGE,{"disambiguationData":[OSD([sQuery(id+"F7.wireOp",EDGE,"E31.top"),sQuery(id+"F7.wireOp",EDGE,"E33.trimOffspring")])]});
            var Q8;
            Q8=makeQuery(id+"F15.opExtrude","SWEPT_EDGE",EDGE,{"disambiguationData":[OSD([sQuery(id+"F14.wireOp",EDGE,"E54.top"),sQuery(id+"F14.wireOp",EDGE,"E54.left")])]});
            var Q9;
            Q9=makeQuery(id+"F15.opExtrude","SWEPT_EDGE",EDGE,{"disambiguationData":[OSD([sQuery(id+"F14.wireOp",EDGE,"E54.bottom"),sQuery(id+"F14.wireOp",EDGE,"E54.left")])]});
            var Q10;
            Q10=makeQuery(id+"F15.opExtrude","SWEPT_EDGE",EDGE,{"disambiguationData":[OSD([sQuery(id+"F14.wireOp",EDGE,"E54.top"),sQuery(id+"F14.wireOp",EDGE,"E54.right")])]});
            var Q11;
            Q11=makeQuery(id+"F15.opExtrude","SWEPT_EDGE",EDGE,{"disambiguationData":[OSD([sQuery(id+"F14.wireOp",EDGE,"E54.bottom"),sQuery(id+"F14.wireOp",EDGE,"E54.right")])]});
            chamfer(context, id + "F18", {"entities" : qUnion([Q0, Q1, Q2, Q3, Q4, Q5, Q6, Q7, Q8, Q9, Q10, Q11]), "width" : 5 * mm, "tangentPropagation" : true});
        }
    });
